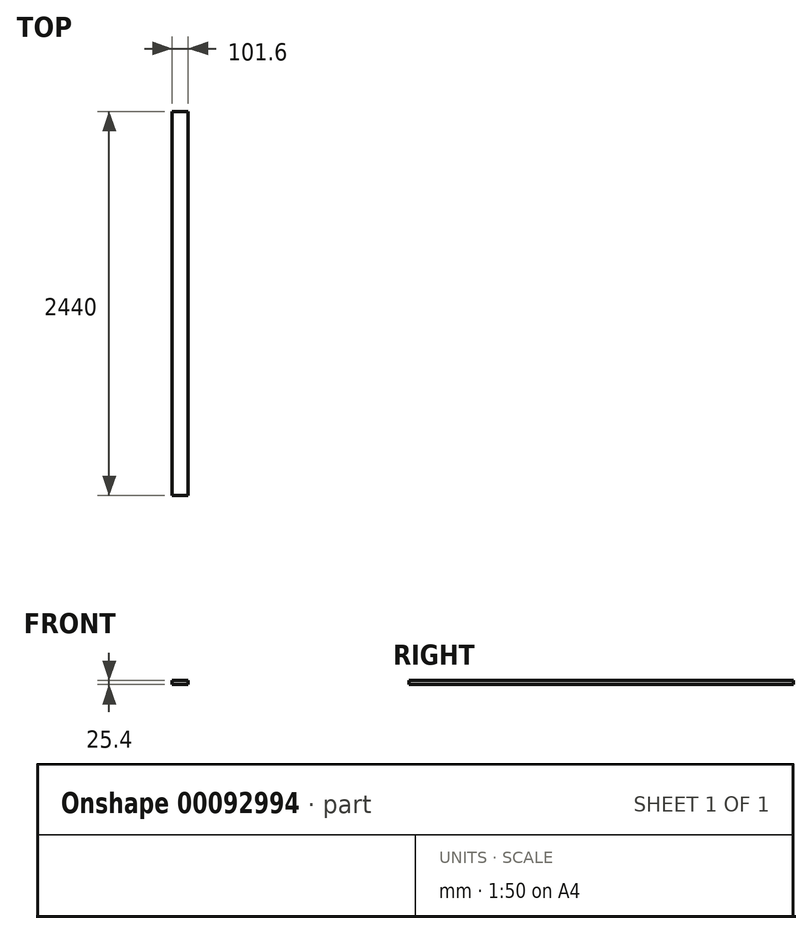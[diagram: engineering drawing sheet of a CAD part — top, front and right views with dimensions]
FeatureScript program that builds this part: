
annotation { "Feature Type Name" : "Feature", "Feature Type Description" : "" }
export const myFeature = defineFeature(function(context is Context, id is Id, definition is map)
    precondition{}
    {
        {
            var Q0;
            Q0=qCreatedBy(makeId("Front.planeOp"),FACE);
            var sketch = newSketch(context, id + "F0", { "sketchPlane" : qUnion([Q0])});
            skLineSegment(sketch, "E0.bottom", {"start": v(-50.8, 25.4) * mm, "end": v(50.8, 25.4) * mm});
            skLineSegment(sketch, "E0.top", {"start": v(-50.8, 0) * mm, "end": v(50.8, 0) * mm});
            skLineSegment(sketch, "E0.left", {"start": v(-50.8, 25.4) * mm, "end": v(-50.8, 0) * mm});
            skLineSegment(sketch, "E0.right", {"start": v(50.8, 25.4) * mm, "end": v(50.8, 0) * mm});
            skSolve(sketch);
        }
        {
            var Q0;
            Q0 = qSketchRegion(id + "F0", true);
            var Q1;
            Q1=makeQuery(id+"F0.imprint","IMPRINT",FACE,{"disambiguationData":[TD([[makeQuery(id+"F0.imprint","IMPRINT",EDGE,{"derivedFrom":sQuery(id+"F0.wireOp",EDGE,"E0.bottom")}),-1.0]])]});
            extrude(context, id + "F1", {"entities" : qUnion([Q0, Q1]), "oppositeDirection" : true, "depth" : 2440 * mm});
        }
    });
